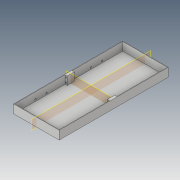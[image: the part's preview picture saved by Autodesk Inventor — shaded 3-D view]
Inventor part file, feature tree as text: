
AUTODESK INVENTOR PART (.ipt)
format: ipt  version: 2019 (Build 230136000, 136)  size: 185,856 bytes
history: native  units: mm
features: sketch x9, extrude x5, hole x4, plane x2, mirror x1, projected_geometry x1
ambient origin geometry x8: Origin, YZ Plane, XZ Plane, XY Plane, X Axis, Y Axis, Z Axis, Center Point
bodies: Solid1 (feature_tree)
feature tree (22):
  sketch  "Sketch1"  dims[d0=295.0mm d1=105.0mm]
  sketch  "Sketch2"  dims[d2=7.6mm d3=3.0mm]
  extrude  "Extrusion1"  Depth=105.0mm
  extrude  "Extrusion2"  Depth=3.0mm
  extrude  "Extrusion4"  Depth=1.0mm TaperAngle=0.0deg
  extrude  "Extrusion6"  Depth=1.0mm
  plane  "Work Plane2"
  plane  "Work Plane4"
  hole  "Hole3"  [1 undecoded]
  hole  "Hole4"  [1 undecoded]
  hole  "Hole5"  [1 undecoded]
  hole  "Hole6"  [1 undecoded]
  mirror  "Mirror6"
  extrude  "Extrusion12"  TaperAngle=150.0deg  [1 undecoded]
  sketch  "Sketch5"  dims[d4=14.0mm d7=1.0mm d8=0.0mm]
  sketch  "Sketch7"  dims[d9=23.0mm d10=1.0mm d11=0.0mm d12=0.0mm d35=4.5mm]
  projected_geometry  "Projected Loop4"
  sketch  "Sketch16"  dims[d37=4.5mm d39=4.5mm]
  sketch  "Sketch17"  dims[d40=0.0mm d41=30.8mm]
  sketch  "Sketch18"  dims[d45=4.5mm d46=0.0mm]
  sketch  "Sketch19"  dims[d47=30.8mm d50=10.0mm d51=0.0mm]
  sketch  "Sketch21"  dims[d57=135.0deg d58=135.0deg d61=6.0mm d62=0.0mm d64=150.0deg d65=150.0deg d71=10.0mm d72=4.0mm d73=10.0mm d74=4.0mm d75=1.5mm d76=60.0mm d77=60.0mm d106=10.0mm d107=10.0mm d108=3.5mm d109=5.0mm d110=2.6mm d111=6.0mm d112=5.0mm d113=2.0mm d114=14.3117mm d115=5.0mm d116=0.0mm d117=2.6mm d118=6.0mm d119=5.0mm d120=2.0mm d121=14.3117mm d122=15.0mm d123=20.594885mm d124=3.5mm d125=5.0mm d126=2.6mm d127=6.0mm d128=5.0mm d129=2.0mm d130=14.3117mm d131=5.0mm d132=0.0mm d133=2.6mm d134=6.0mm d135=5.0mm d136=2.0mm d137=14.3117mm d138=15.0mm d139=20.594885mm d142=5.2mm d143=0.0mm d144=18.0mm d145=18.0mm d148=151.5mm d149=151.5mm d91=1.0mm d92=1.0mm d93=1.0mm d94=0.15mm d95=0.25mm d96=0.375mm d97=14.3117mm d98=0.75mm d99=20.594885mm d100=0.0625mm d101=0.75mm d102=0.375mm]
note: 5 required parameter values undecoded (feature->parameter linkage not recoverable at this tier; creation-order binding heuristic only, values carry confidence <= 0.55)
